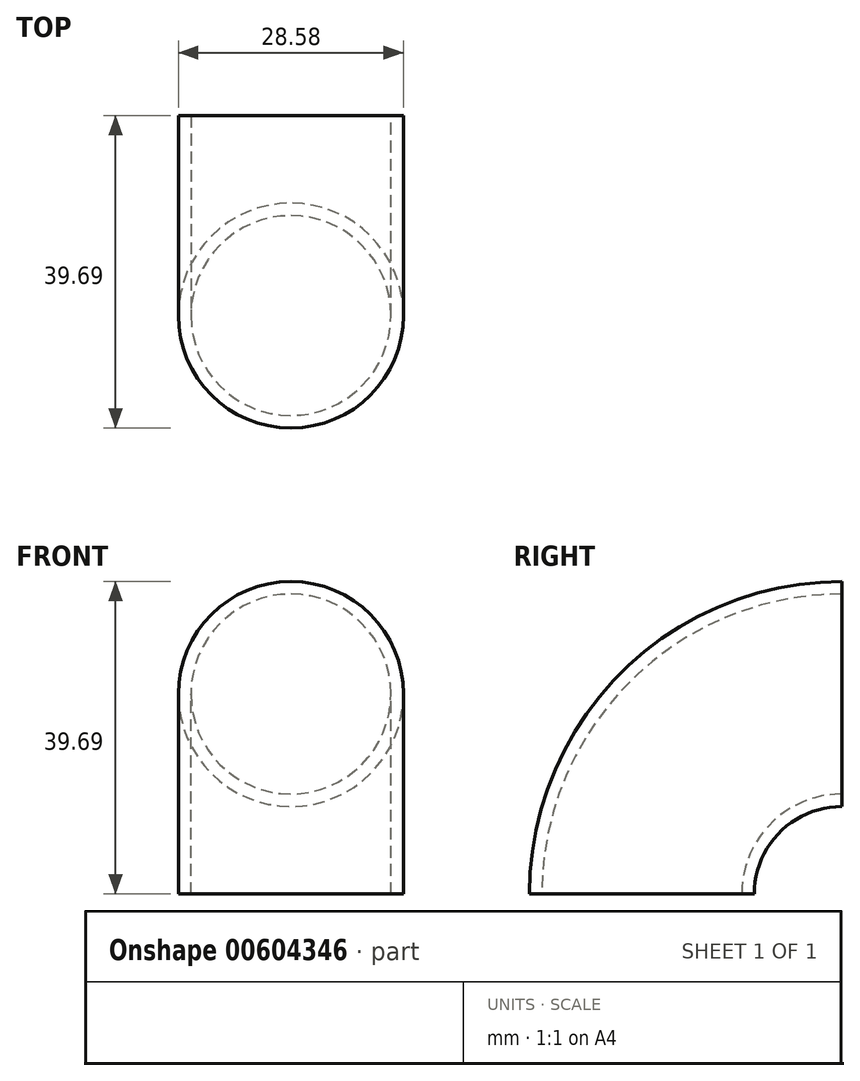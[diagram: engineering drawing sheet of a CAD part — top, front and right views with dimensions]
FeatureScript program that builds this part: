
annotation { "Feature Type Name" : "Feature", "Feature Type Description" : "" }
export const myFeature = defineFeature(function(context is Context, id is Id, definition is map)
    precondition{}
    {
        {
            var Q0;
            Q0=qCreatedBy(makeId("Top.planeOp"),FACE);
            var sketch = newSketch(context, id + "F0", { "sketchPlane" : qUnion([Q0])});
            skLineSegment(sketch, "E0", {"start": v(0, 0) * mm, "end": v(12.7, 0) * mm});
            skCircle(sketch, "E1", {"center": v(0, 0) * mm, "radius": 12.7 * mm});
            skCircle(sketch, "E2.0", {"center": v(0, 0) * mm, "radius": 14.29 * mm});
            skSolve(sketch);
        }
        {
            var Q0;
            Q0=qCreatedBy(makeId("Right.planeOp"),FACE);
            var sketch = newSketch(context, id + "F1", { "sketchPlane" : qUnion([Q0])});
            skLineSegment(sketch, "E3", {"start": v(0, 0) * mm, "end": v(0, 0) * mm});
            skLineSegment(sketch, "E4", {"start": v(0, 0) * mm, "end": v(25.4, 0) * mm});
            skArc(sketch, "E5", {"start": v(0, 0) * mm, "mid": v(7.44, 17.96) * mm, "end": v(25.4, 25.4) * mm});
            skSolve(sketch);
        }
        {
            var Q0;
            Q0=qSketchRegion(id+"F0",true);
            var Q1;
            Q1=sQuery(id+"F1.wireOp",EDGE,"E5");
            sweep(context, id + "F2", {"profiles" : qUnion([Q0]), "path" : qUnion([Q1])});
        }
    });
